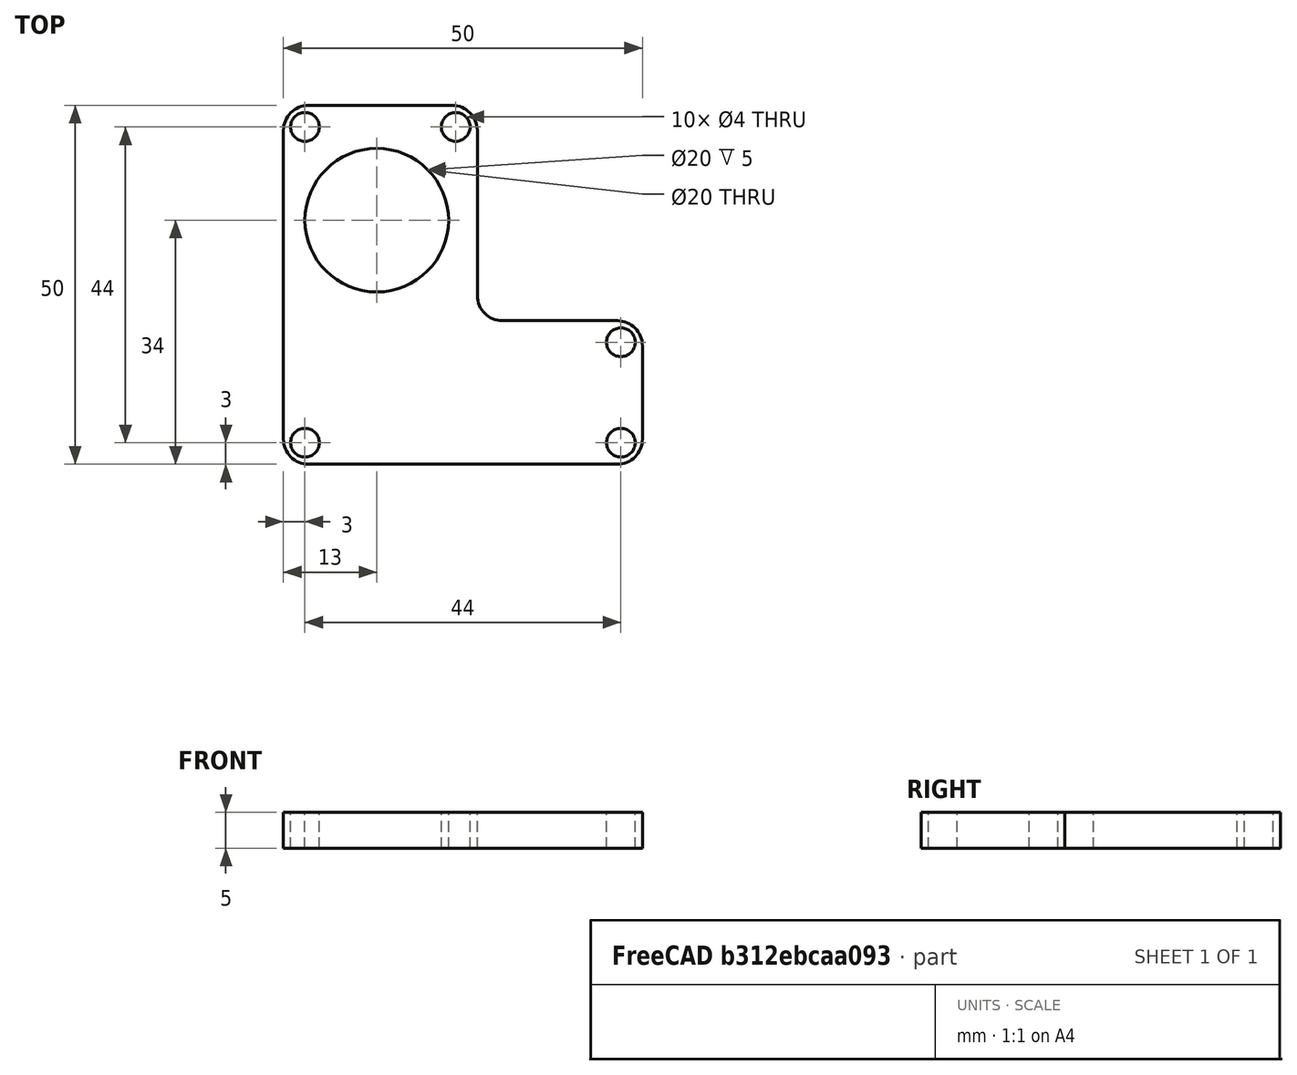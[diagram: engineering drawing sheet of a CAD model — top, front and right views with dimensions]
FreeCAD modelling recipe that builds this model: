
FCSTD DOCUMENT  (FreeCAD 0.17R13523 (Git))
Label: motormount
License: All rights reserved
LicenseURL: http://en.wikipedia.org/wiki/All_rights_reserved
objects: Part::Cylinder×6, Part::Box×2, Part::Fuse×1, Part::MultiFuse×1, Part::Cut×1, Part::Fillet×1, Part::Feature×1
note: 13 computed .brp shape members not serialized (recipe doc carries the construction recipe); baked Part::Feature solids carry a one-line shape summary decoded from their .brp

FEATURE [Part::Box] Box  label="Cube"
  AttacherType = Attacher::AttachEngine3D
  Height = 5
  Length = 27
  Width = 50
FEATURE [Part::Box] Box001  label="Cube001"
  AttacherType = Attacher::AttachEngine3D
  Height = 5
  Length = 50
  Width = 20
FEATURE [Part::Fuse] Fusion
  Base = -> Box
  Tool = -> Box001
FEATURE [Part::Cylinder] Cylinder
  Angle = 360
  AttacherType = Attacher::AttachEngine3D
  Height = 10
  Placement = pos=(47,17,0) rot=(0,0,1;0rad)
  Radius = 2
FEATURE [Part::Cylinder] Cylinder001
  Angle = 360
  AttacherType = Attacher::AttachEngine3D
  Height = 10
  Placement = pos=(47,3,0) rot=(0,0,1;0rad)
  Radius = 2
FEATURE [Part::Cylinder] Cylinder002
  Angle = 360
  AttacherType = Attacher::AttachEngine3D
  Height = 10
  Placement = pos=(3,3,0) rot=(0,0,1;0rad)
  Radius = 2
FEATURE [Part::Cylinder] Cylinder003
  Angle = 360
  AttacherType = Attacher::AttachEngine3D
  Height = 10
  Placement = pos=(3,47,0) rot=(0,0,1;0rad)
  Radius = 2
FEATURE [Part::Cylinder] Cylinder004
  Angle = 360
  AttacherType = Attacher::AttachEngine3D
  Height = 10
  Placement = pos=(24,47,0) rot=(0,0,1;0rad)
  Radius = 2
FEATURE [Part::Cylinder] Cylinder005
  Angle = 360
  AttacherType = Attacher::AttachEngine3D
  Height = 10
  Placement = pos=(13,34,0) rot=(0,0,1;0rad)
  Radius = 10
FEATURE [Part::MultiFuse] Fusion001
  Shapes = -> [Cylinder,Cylinder004,Cylinder003,Cylinder005,Cylinder002,Cylinder001]
FEATURE [Part::Cut] Cut
  Base = -> Fusion
  Tool = -> Fusion001
FEATURE [Part::Fillet] Fillet
  Base = -> Cut
  Edges = 6 edges r=3.5: [Edge2,Edge4,Edge12,Edge27,Edge33,Edge40]
FEATURE [Part::Feature] Fillet001
  shape: bbox 50 x 50 x 5 mm, 20 faces (baked)
